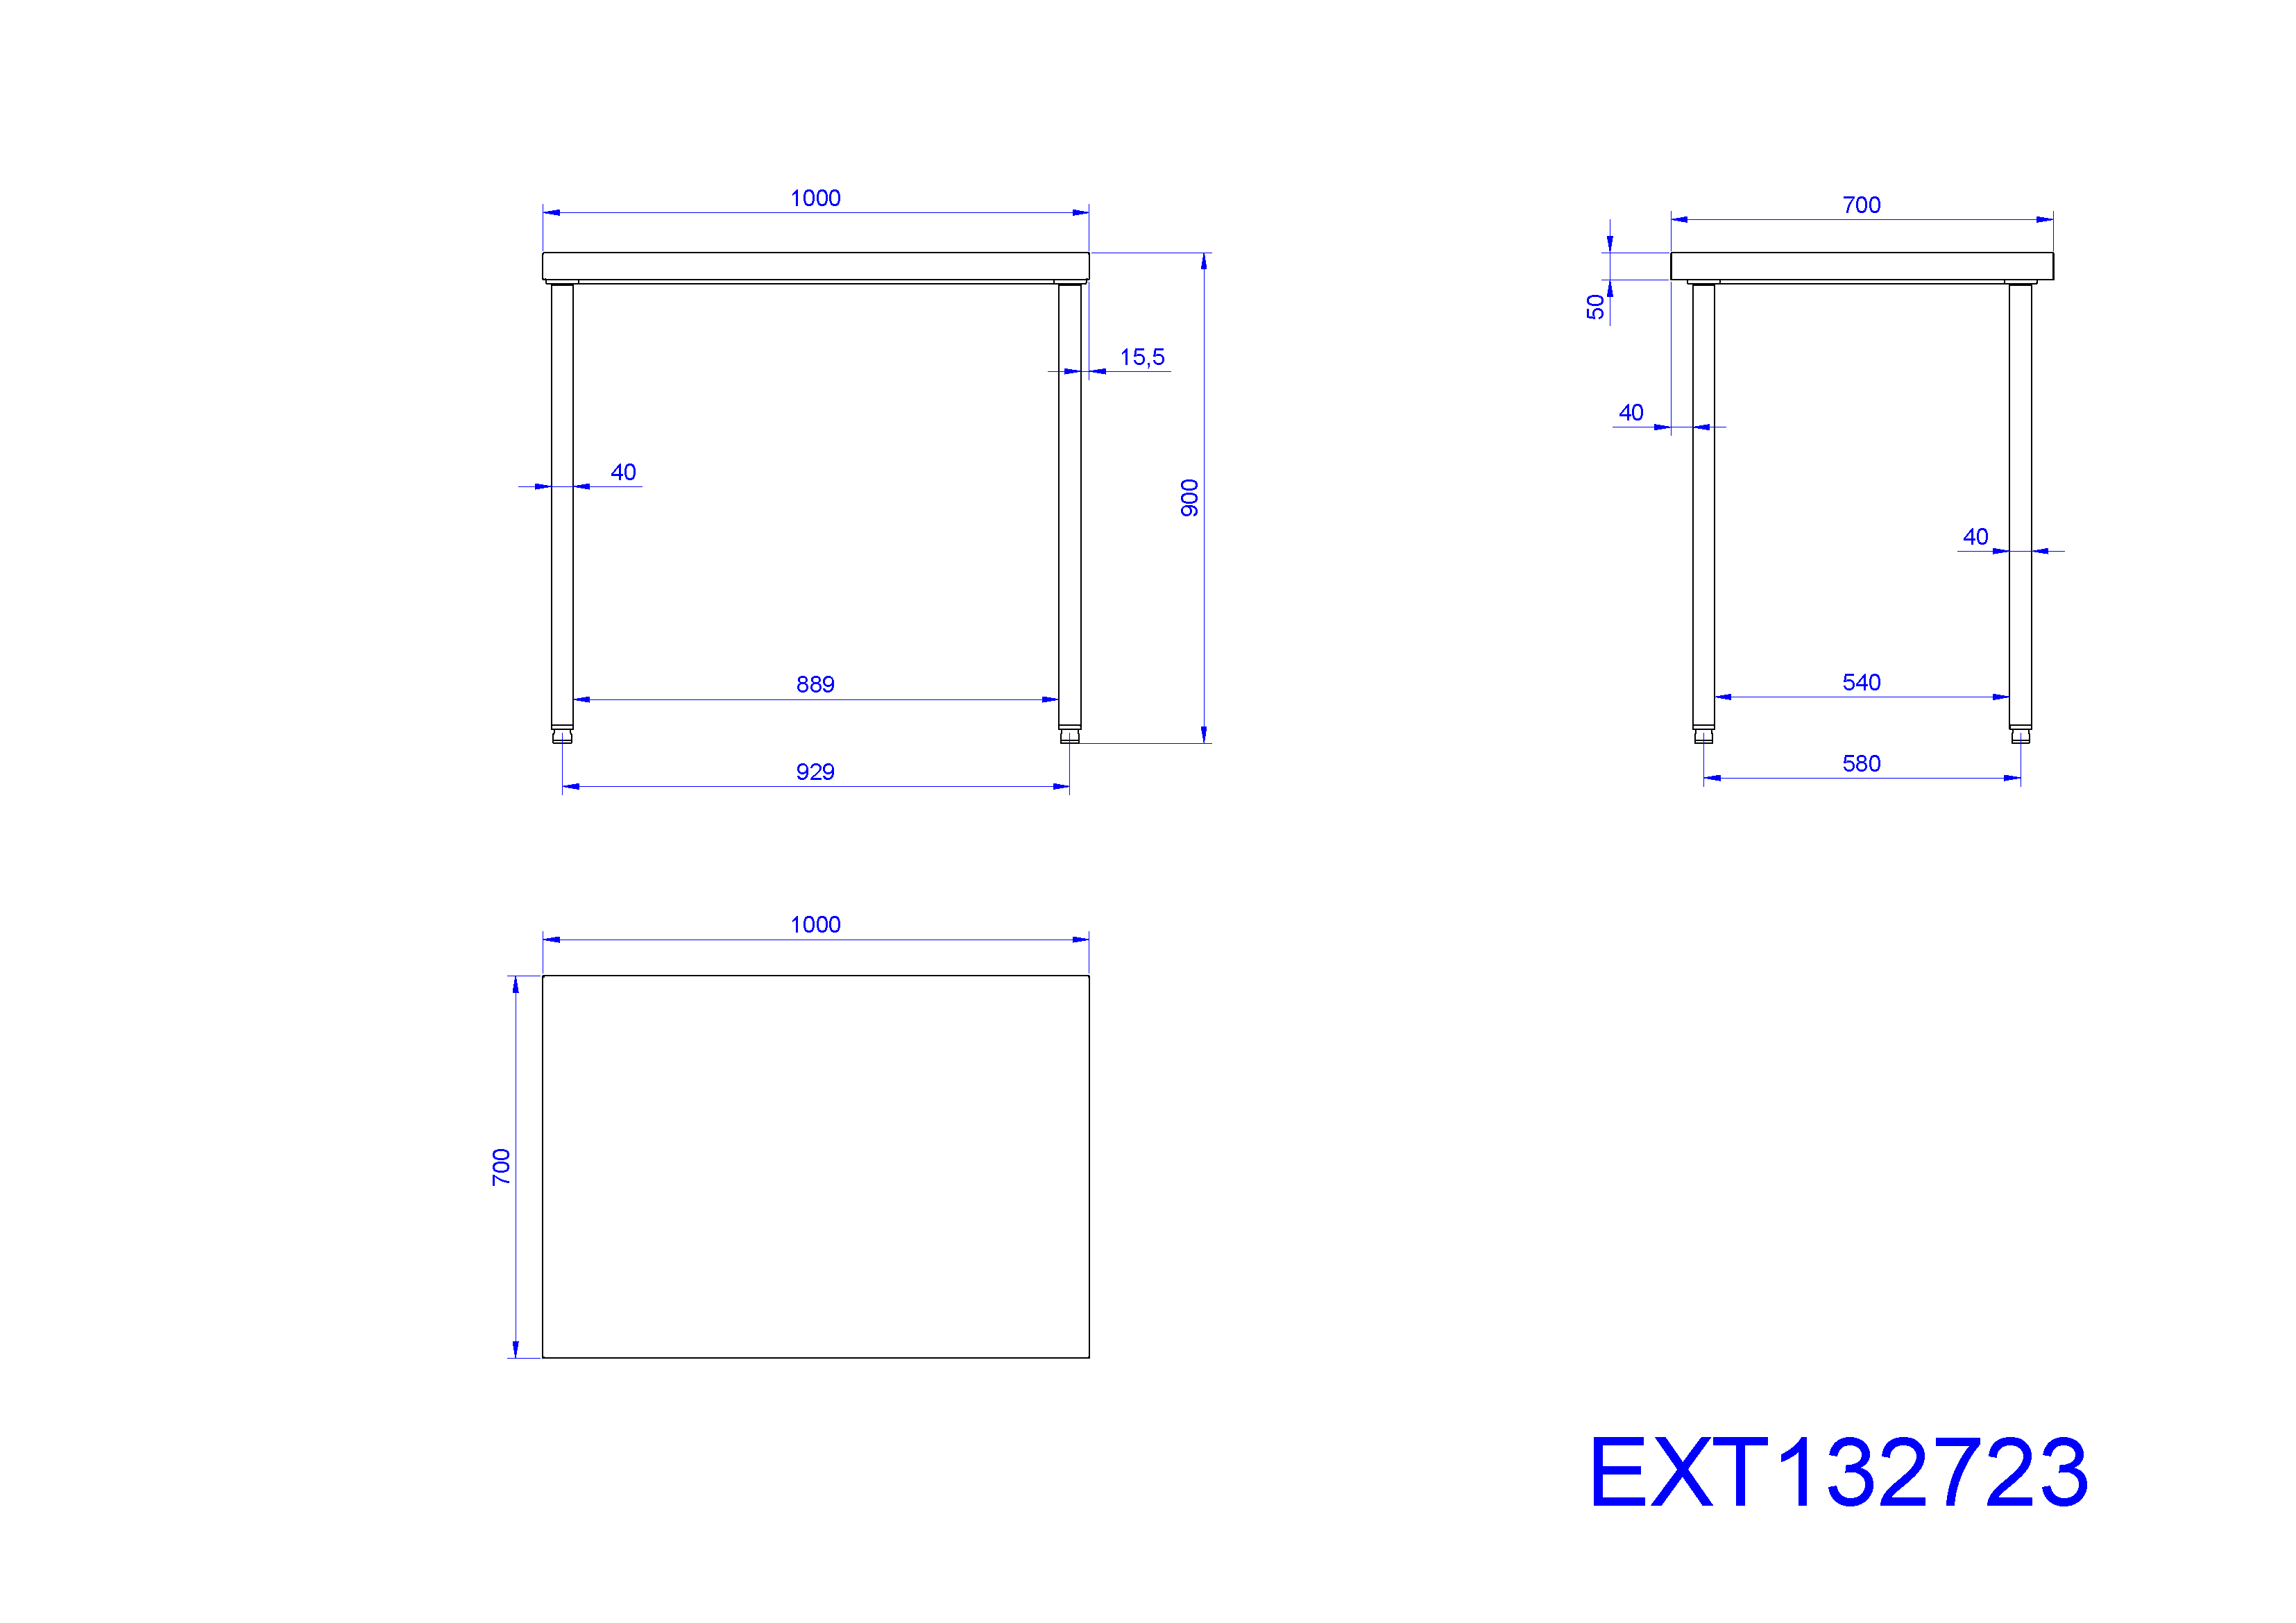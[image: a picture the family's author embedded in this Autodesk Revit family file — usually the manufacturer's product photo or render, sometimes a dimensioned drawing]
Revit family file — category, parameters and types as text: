
# Revit family: QF_ELECTROLUXPROFESSIONAL_134132_GLG716P
name_source: partatom
category: Attrezzature speciali
units: mm (PartAtom-declared; Revit-internal decimal feet)

## family parameters
Basato su piano di lavoro = No
Condiviso = No
Punto di calcolo locali = No
Quota connettore circolare = Usa diametro
Sempre verticale = Sì
Taglio con vuoti quando caricato = No
Tipo di parte = Normale

## types (1)
- Standard
    Accessory = Sì
    Cold Water Size = 0 mm
    Compressed Air Pressure = 0.0 Pa
    Compressed Air Size = 0 mm
    Compressed Air Volume = 0.0 L/s
    Condensate Return Size = 0 mm
    Cycle = 0 Hz
    Depth Actual = 700 mm  [stored 2.29659 ft]
    Descrizione = SINK CUPBOARD 1 BOWL 700 MM
    Direct Waste Size = 0 mm
    Gas Input Pressure = 0
    Gas KW = 0
    Gas Size = 0 mm
    HP = 0 HP
    Height Actual = 1000 mm  [stored 3.28084 ft]
    Hot Water Size = 0 mm
    Item Number = 134132
    Length Actual = 700 mm  [stored 2.29659 ft]
    Modello = GLG716P
    Phase = 0
    Produttore = Electrolux Professional
    Prospetto di default = 0 mm  [stored 0 ft]
    Refrigerant Compressor Remote = Sì
    Refrigeration Liquid Line Size = 0 mm  [stored 0 ft]
    Refrigeration Suction Line Size = 0 mm  [stored 0 ft]
    Steam Consumption per Hour = 0
    Steam Supply Maximum Pressure = 0.0 Pa
    Steam Supply Minimum Pressure = 0.0 Pa
    Steam Supply Size = 0 mm
    URL = https://www.electroluxprofessional.com
    URL Manufacturer = https://www.electroluxprofessional.com
    Volts = 0 V
    Watts = 0 W
    Weight = 34.00 kg

note: source unit labels omitted for Gas Input Pressure — the stored unit's dimension contradicts the parameter name (converter mislabeling)

note: [stored X ft] marks values corroborated as IEEE doubles in the binary element streams (Revit-internal decimal feet)

## geometry (parser evidence)
native form markers: Sweep x5
no freeform markers — native parametric forms only
